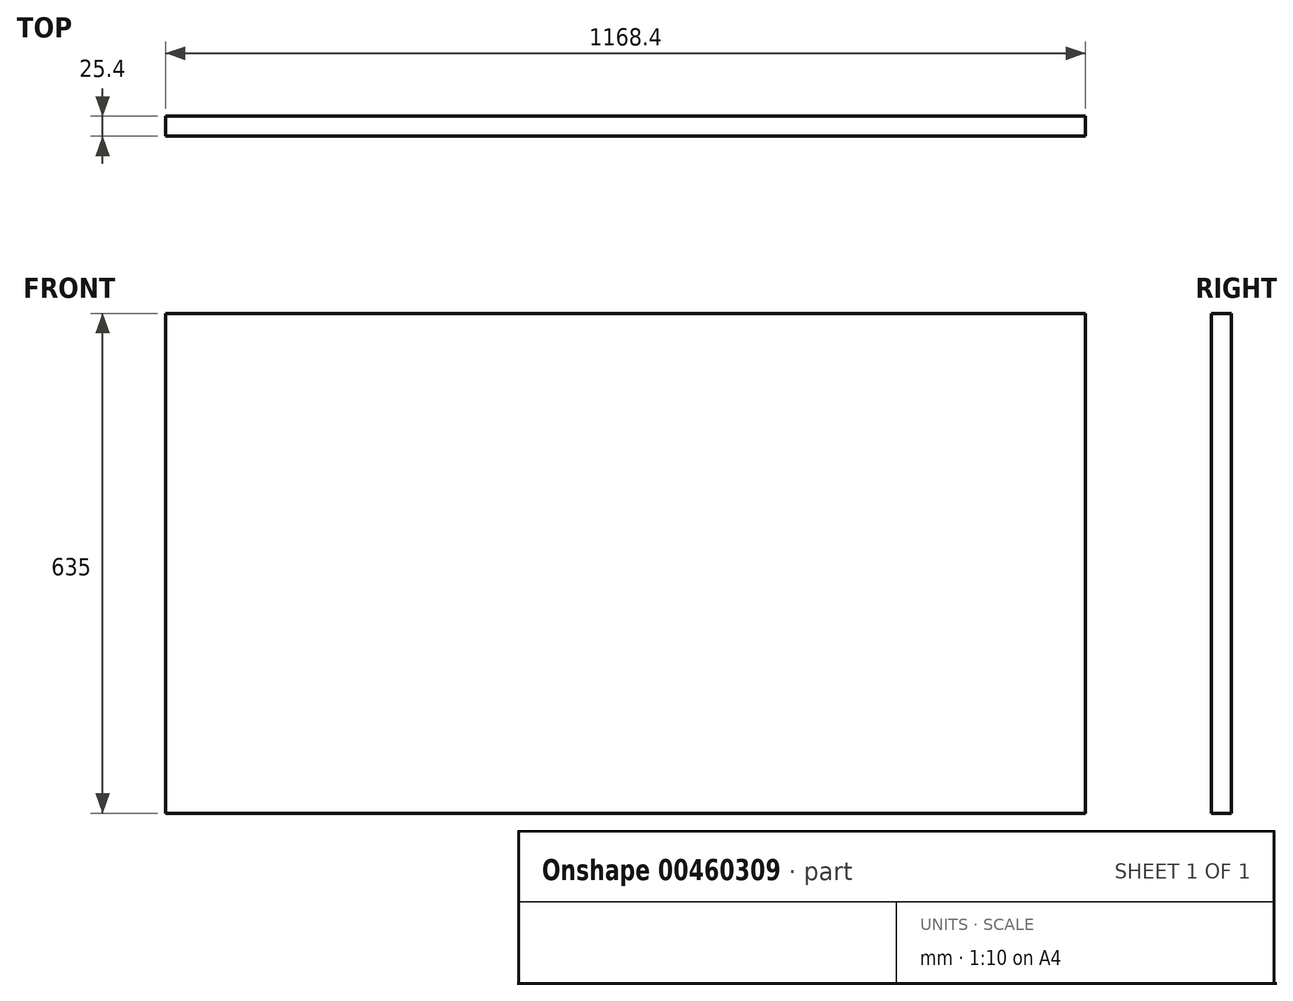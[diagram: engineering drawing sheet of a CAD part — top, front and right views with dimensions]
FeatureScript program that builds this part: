
annotation { "Feature Type Name" : "Feature", "Feature Type Description" : "" }
export const myFeature = defineFeature(function(context is Context, id is Id, definition is map)
    precondition{}
    {
        {
            var Q0;
            Q0=qCreatedBy(makeId("Front.planeOp"),FACE);
            var sketch = newSketch(context, id + "F0", { "sketchPlane" : qUnion([Q0])});
            skLineSegment(sketch, "E0.bottom", {"start": v(-584.2, 317.5) * mm, "end": v(584.2, 317.5) * mm});
            skLineSegment(sketch, "E0.top", {"start": v(-584.2, -317.5) * mm, "end": v(584.2, -317.5) * mm});
            skLineSegment(sketch, "E0.left", {"start": v(-584.2, 317.5) * mm, "end": v(-584.2, -317.5) * mm});
            skLineSegment(sketch, "E0.right", {"start": v(584.2, 317.5) * mm, "end": v(584.2, -317.5) * mm});
            skSolve(sketch);
        }
        {
            var Q0;
            Q0 = qSketchRegion(id + "F0", true);
            extrude(context, id + "F1", {"entities" : qUnion([Q0]), "depth" : 25.4 * mm});
        }
    });
